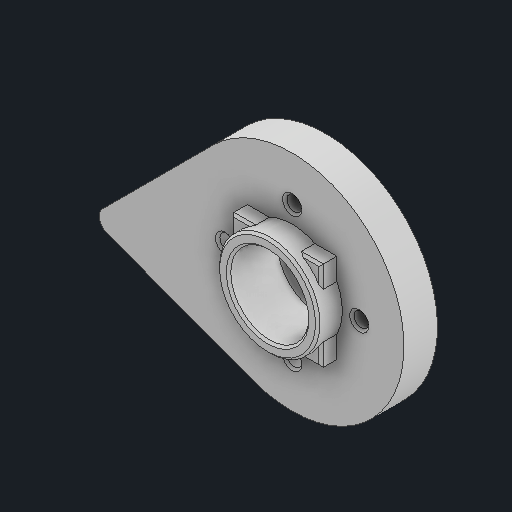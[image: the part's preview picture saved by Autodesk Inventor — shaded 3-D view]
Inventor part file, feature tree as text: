
AUTODESK INVENTOR PART (.ipt)
format: ipt  version: 2024.1 (Build 281209000, 209)  size: 211,456 bytes
history: native  units: in
note: dims shown in document units (in); Inventor stores cm internally (conversion verified against a paired STEP export)
features: extrude x5, other x3, plane x1, sketch x1, chamfer x1, reference x1
ambient origin geometry x8: Origin, YZ Plane, XZ Plane, XY Plane, X Axis, Y Axis, Z Axis, Center Point
bodies: Solid1 (feature_tree)
feature tree (12):
  plane  "Work Plane1"
  sketch  "Sketch1"  dims[d0=0.003in d1=2.5in d2=1.0in d3=1.0in d4=0.1654in d5=0.75in d6=1.5748in d8=360.0deg d10=0.125in d11=0.6498in d12=0.0in d13=0.375in d14=0.0in d15=0.3425in d16=0.0986in d17=0.0in d18=0.55in d19=0.0in d20=0.025in d21=0.125in d22=45.0deg d23=0.25in d24=0.375in d25=0.0in]
  extrude  "Extrusion1"  Depth=0.375in
  extrude  "Extrusion2"  Depth=1.0in
  extrude  "Extrusion3"  Depth=1.0in
  extrude  "Extrusion4"  Depth=0.375in
  chamfer  "Chamfer1"  Distance=0.75in
  extrude  "Extrusion5"  Depth=0.375in TaperAngle=360.0deg
  reference  "Reference1"
  other  "<userpath>\Documents\School\FallCAD\Trebuchet\Trebuchet.iam"
  other  "Trebuchet.iam"
  other  "BallBearing_8x22x7mm:6"
